# Revit family: 208_USUF  _
name_source: partatom
category: Air Terminals
units: mm (PartAtom-declared; Revit-internal decimal feet)

## family parameters
Always vertical = Yes
Cut with Voids When Loaded = No
Part Type = Normal
Room Calculation Point = Yes
Round Connector Dimension = Use Diameter
Shared = No
Work Plane-Based = No

## types (3) — shared parameters
CL_Location_5000 = 5000 mm  [stored 16.4042 ft]
Description = EXTERNAL GRILL
L1 = 10 mm  [stored 0.0328084 ft]
L2 = 52 mm  [stored 0.170604 ft]
L_ARR = 400 mm  [stored 1.31234 ft]
Manufacturer = Alnor
QmdConnectorList = 201;D
URL = http://www.ventilation-alnor.co.uk
W_ARR = 400 mm  [stored 1.31234 ft]
XRefLineVPlnId = 7453
YRefLineVPlnId = 7456
magiPartTypeId = 208
magiProductFamilyId = USUF  *
zero-valued in all types: CLBTZ, H_ARR

## per-type parameters (varying)
| type | B1 | BGD | D | R | R1 |
| USUF  100 | 79 mm | 71 mm | 100 mm | 50 mm  [stored 0.164042 ft] | 58 mm  [stored 0.190289 ft] |
| USUF  150 | 108 mm | 100 mm  [stored 0.328084 ft] | 150 mm | 75 mm | 83 mm |
| USUF  125 | 95 mm | 87 mm | 125 mm | 63 mm | 71 mm |

note: column(s) folded — value = type name in every type: MC Product Code, magiProductId

note: [stored X ft] marks values corroborated as IEEE doubles in the binary element streams (Revit-internal decimal feet)

## geometry (parser evidence)
native form markers: Blend x4, Sweep x2
no freeform markers — native parametric forms only
